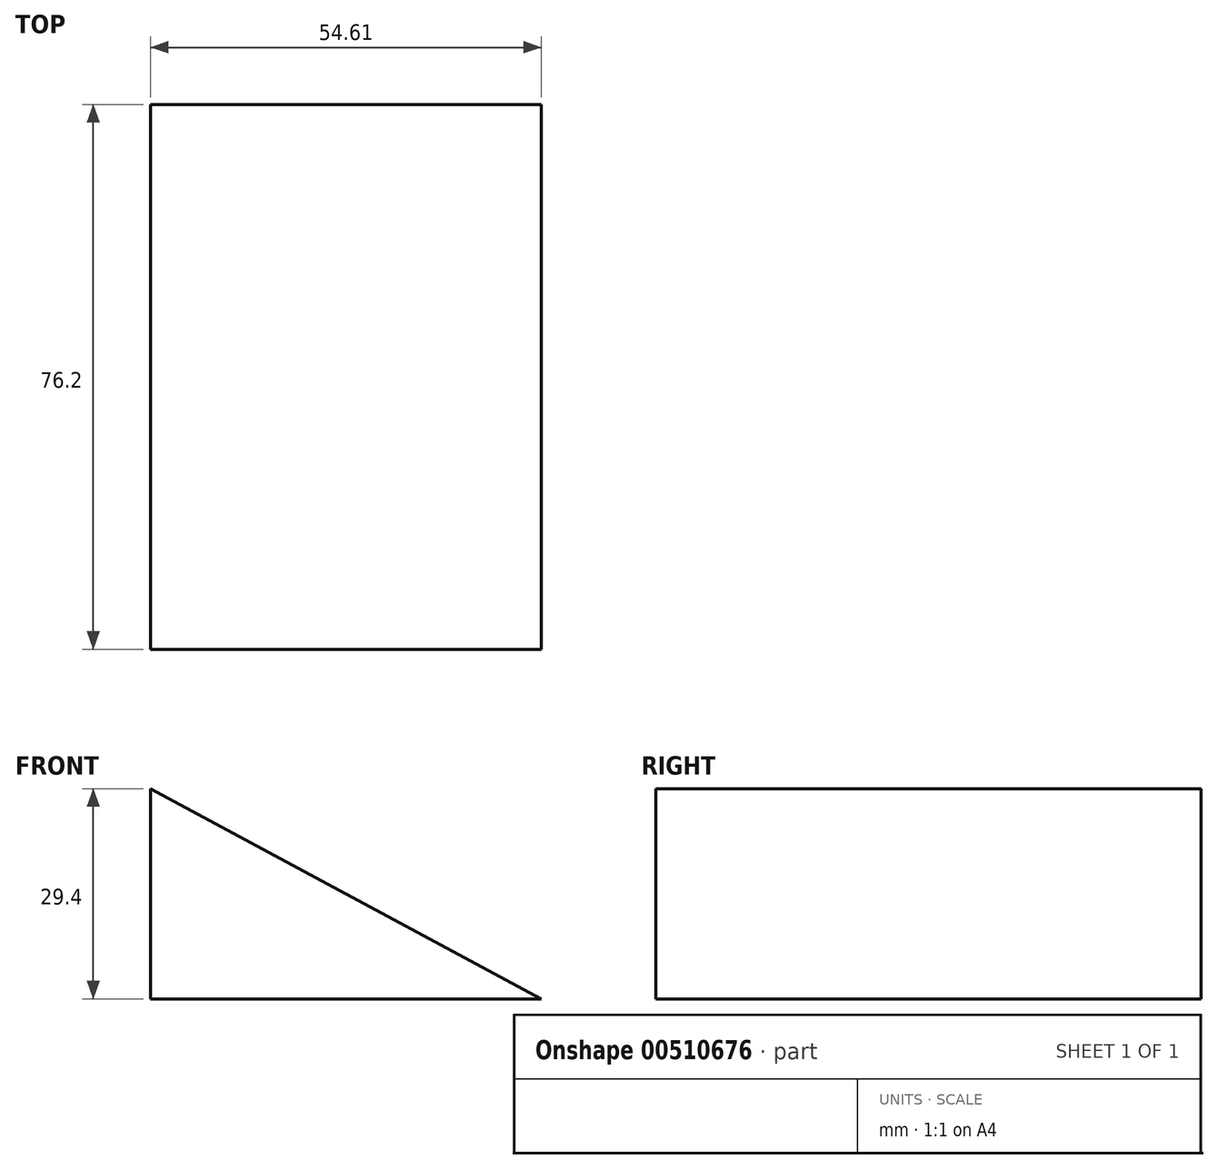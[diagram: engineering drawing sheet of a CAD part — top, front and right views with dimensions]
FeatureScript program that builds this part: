
annotation { "Feature Type Name" : "Feature", "Feature Type Description" : "" }
export const myFeature = defineFeature(function(context is Context, id is Id, definition is map)
    precondition{}
    {
        {
            var Q0;
            Q0=qCreatedBy(makeId("Front.planeOp"),FACE);
            var sketch = newSketch(context, id + "F0", { "sketchPlane" : qUnion([Q0])});
            skLineSegment(sketch, "E0", {"start": v(-34.55, 28.08) * mm, "end": v(-34.55, -1.32) * mm});
            skLineSegment(sketch, "E1", {"start": v(-34.55, -1.32) * mm, "end": v(20.06, -1.32) * mm});
            skLineSegment(sketch, "E2", {"start": v(-34.55, 28.08) * mm, "end": v(20.06, -1.32) * mm});
            skSolve(sketch);
        }
        {
            var Q0;
            Q0 = qSketchRegion(id + "F0", true);
            extrude(context, id + "F1", {"entities" : qUnion([Q0]), "depth" : 76.2 * mm});
        }
    });
